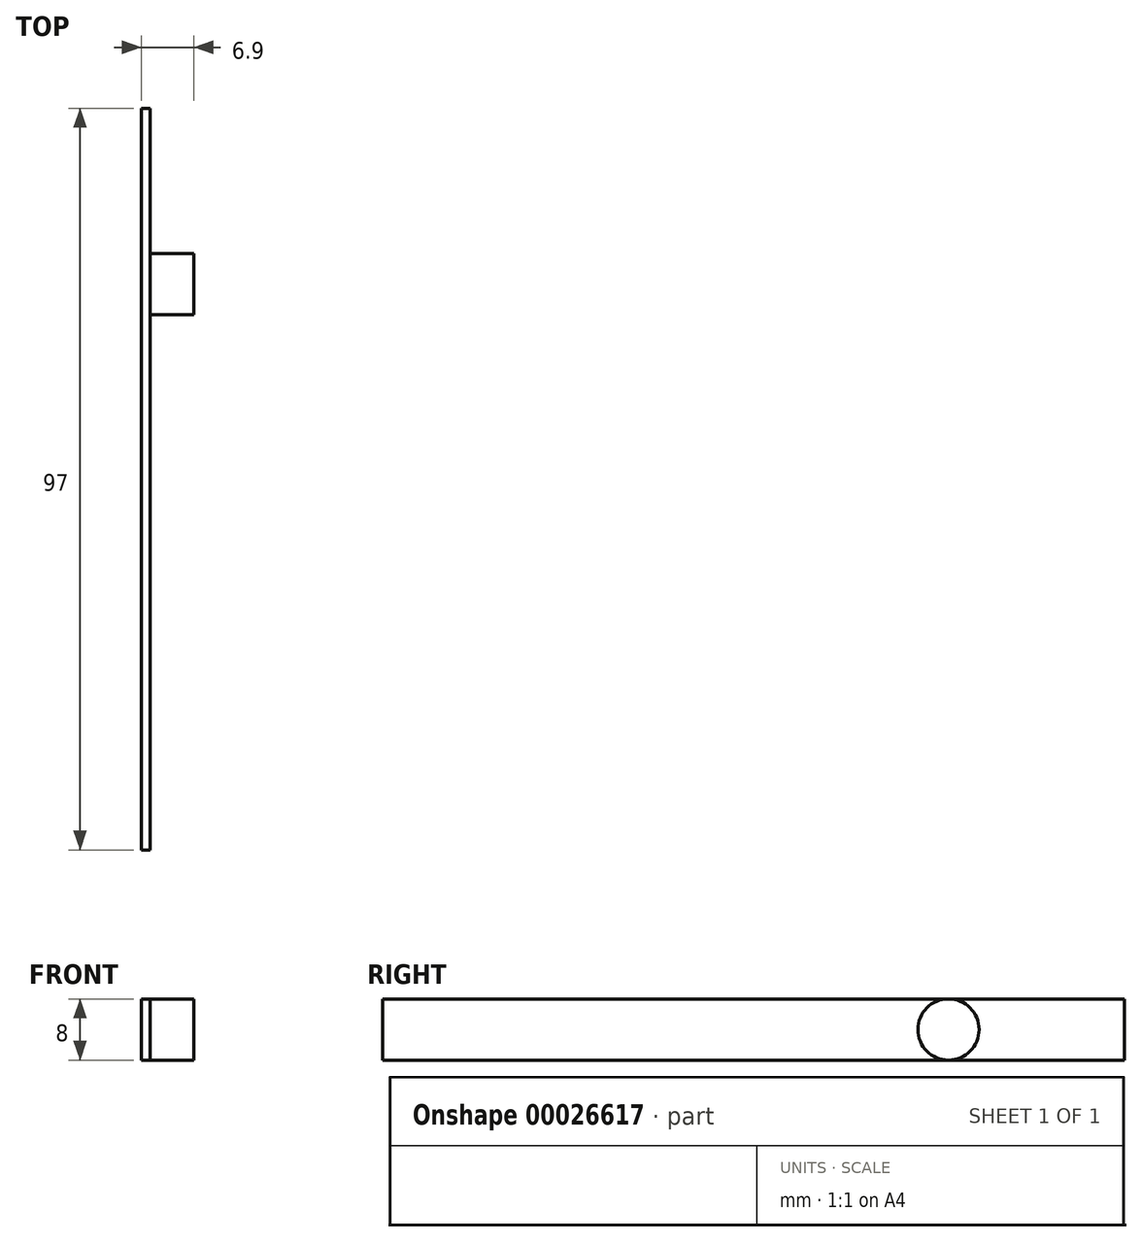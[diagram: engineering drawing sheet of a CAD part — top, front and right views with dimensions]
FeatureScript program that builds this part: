
annotation { "Feature Type Name" : "Feature", "Feature Type Description" : "" }
export const myFeature = defineFeature(function(context is Context, id is Id, definition is map)
    precondition{}
    {
        {
            var Q0;
            Q0=qCreatedBy(makeId("Right.planeOp"),FACE);
            var sketch = newSketch(context, id + "F0", { "sketchPlane" : qUnion([Q0])});
            skLineSegment(sketch, "E0.bottom", {"start": v(-3, 0) * mm, "end": v(27, 0) * mm});
            skLineSegment(sketch, "E0.top", {"start": v(-3, -8) * mm, "end": v(27, -8) * mm});
            skLineSegment(sketch, "E0.right", {"start": v(27, 0) * mm, "end": v(27, -8) * mm});
            skLineSegment(sketch, "E1", {"start": v(-9.82, -8) * mm, "end": v(-9.82, -4) * mm, "construction": true});
            skLineSegment(sketch, "E2", {"start": v(-9.82, -4) * mm, "end": v(27, -4) * mm, "construction": true});
            skArc(sketch, "E3", {"start": v(-3, 0) * mm, "mid": v(-7, -4) * mm, "end": v(-3, -8) * mm});
            skPoint(sketch, "E4.orphan", {"position": v(0, -8) * mm});
            skLineSegment(sketch, "E5", {"start": v(-3, 0) * mm, "end": v(-7, 0) * mm});
            skLineSegment(sketch, "E6", {"start": v(-7, 0) * mm, "end": v(-7, -8) * mm});
            skLineSegment(sketch, "E7", {"start": v(-7, -8) * mm, "end": v(-3, -8) * mm});
            skLineSegment(sketch, "E8", {"start": v(-7, 0) * mm, "end": v(-70, 0) * mm});
            skLineSegment(sketch, "E9", {"start": v(-70, 0) * mm, "end": v(-70, -8) * mm});
            skLineSegment(sketch, "E10", {"start": v(-70, -8) * mm, "end": v(-7, -8) * mm});
            skSolve(sketch);
        }
        {
            var Q0;
            Q0 = qSketchRegion(id + "F0", true);
            extrude(context, id + "F1", {"entities" : qUnion([Q0]), "depth" : 1.2 * mm});
        }
        {
            var Q0;
            Q0=makeQuery(id+"F1.opExtrude","CAP_FACE",FACE,{"disambiguationData":[OSD([sQuery(id+"F0.wireOp",EDGE,"E0.bottom"),sQuery(id+"F0.wireOp",EDGE,"E0.top"),sQuery(id+"F0.wireOp",EDGE,"E0.right"),sQuery(id+"F0.wireOp",EDGE,"E3")])],"isStart":false});
            var sketch = newSketch(context, id + "F2", { "sketchPlane" : qUnion([Q0])});
            skLineSegment(sketch, "E11", {"start": v(27, 0) * mm, "end": v(27, -8) * mm, "construction": true});
            skLineSegment(sketch, "E12", {"start": v(0, -4) * mm, "end": v(4, -4) * mm, "construction": true});
            skCircle(sketch, "E13", {"center": v(4, -4) * mm, "radius": 4 * mm});
            skSolve(sketch);
        }
        {
            var Q0;
            Q0 = qSketchRegion(id + "F2", true);
            extrude(context, id + "F3", {"entities" : qUnion([Q0]), "operationType" : NewBodyOperationType.ADD, "depth" : 5.7 * mm});
        }
    });
